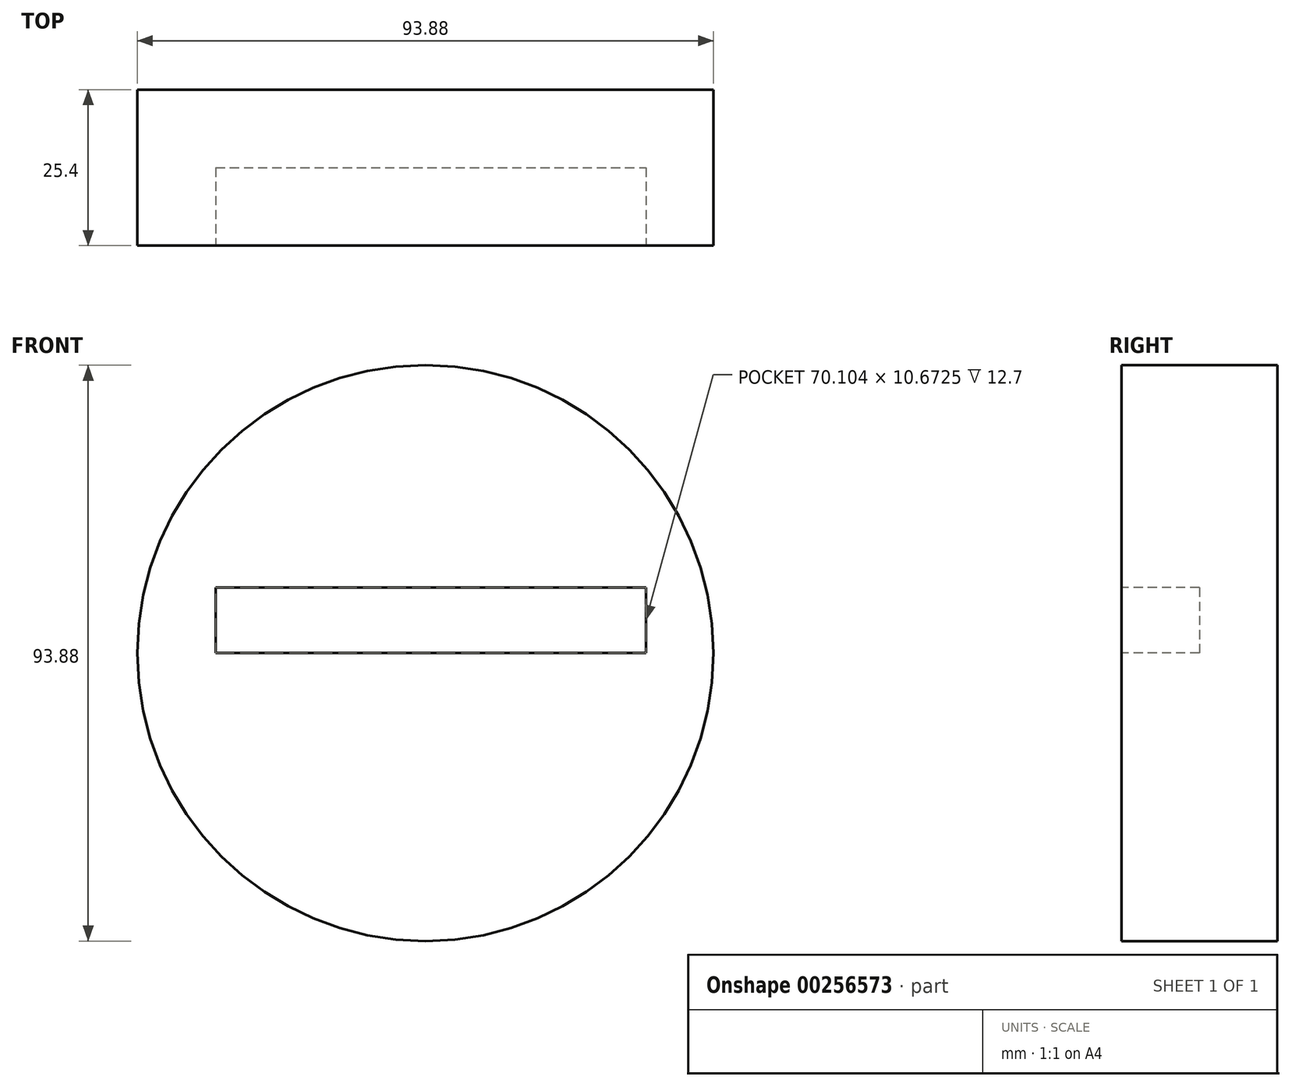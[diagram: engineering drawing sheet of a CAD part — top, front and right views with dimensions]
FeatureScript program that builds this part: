
annotation { "Feature Type Name" : "Feature", "Feature Type Description" : "" }
export const myFeature = defineFeature(function(context is Context, id is Id, definition is map)
    precondition{}
    {
        {
            var Q0;
            Q0=qCreatedBy(makeId("Front.planeOp"),FACE);
            var sketch = newSketch(context, id + "F0", { "sketchPlane" : qUnion([Q0])});
            skCircle(sketch, "E0", {"center": v(0, 0) * mm, "radius": 46.94 * mm});
            skSolve(sketch);
        }
        {
            var Q0;
            Q0=makeQuery(id+"F0.imprint","IMPRINT",FACE,{"disambiguationData":[TD([[makeQuery(id+"F0.imprint","IMPRINT",EDGE,{"derivedFrom":sQuery(id+"F0.wireOp",EDGE,"E0")}),1.0]])]});
            extrude(context, id + "F1", {"entities" : qUnion([Q0]), "depth" : 25.4 * mm});
        }
        {
            var Q0;
            Q0=makeQuery(id+"F1.opExtrude","CAP_FACE",FACE,{"disambiguationData":[OSD([sQuery(id+"F0.wireOp",EDGE,"E0")])],"isStart":false});
            var sketch = newSketch(context, id + "F2", { "sketchPlane" : qUnion([Q0])});
            skLineSegment(sketch, "E1.bottom", {"start": v(-34.17, 10.67) * mm, "end": v(35.94, 10.67) * mm});
            skLineSegment(sketch, "E1.top", {"start": v(-34.17, 0) * mm, "end": v(35.94, 0) * mm});
            skLineSegment(sketch, "E1.left", {"start": v(-34.17, 10.67) * mm, "end": v(-34.17, 0) * mm});
            skLineSegment(sketch, "E1.right", {"start": v(35.94, 10.67) * mm, "end": v(35.94, 0) * mm});
            skSolve(sketch);
        }
        {
            var Q0;
            Q0=makeQuery(id+"F2.imprint","IMPRINT",FACE,{"disambiguationData":[TD([[makeQuery(id+"F2.imprint","IMPRINT",EDGE,{"derivedFrom":sQuery(id+"F2.wireOp",EDGE,"E1.bottom")}),-1.0]])]});
            extrude(context, id + "F3", {"entities" : qUnion([Q0]), "operationType" : NewBodyOperationType.REMOVE, "endBound" : BoundingType.SYMMETRIC, "oppositeDirection" : true, "depth" : 25.4 * mm});
        }
    });
